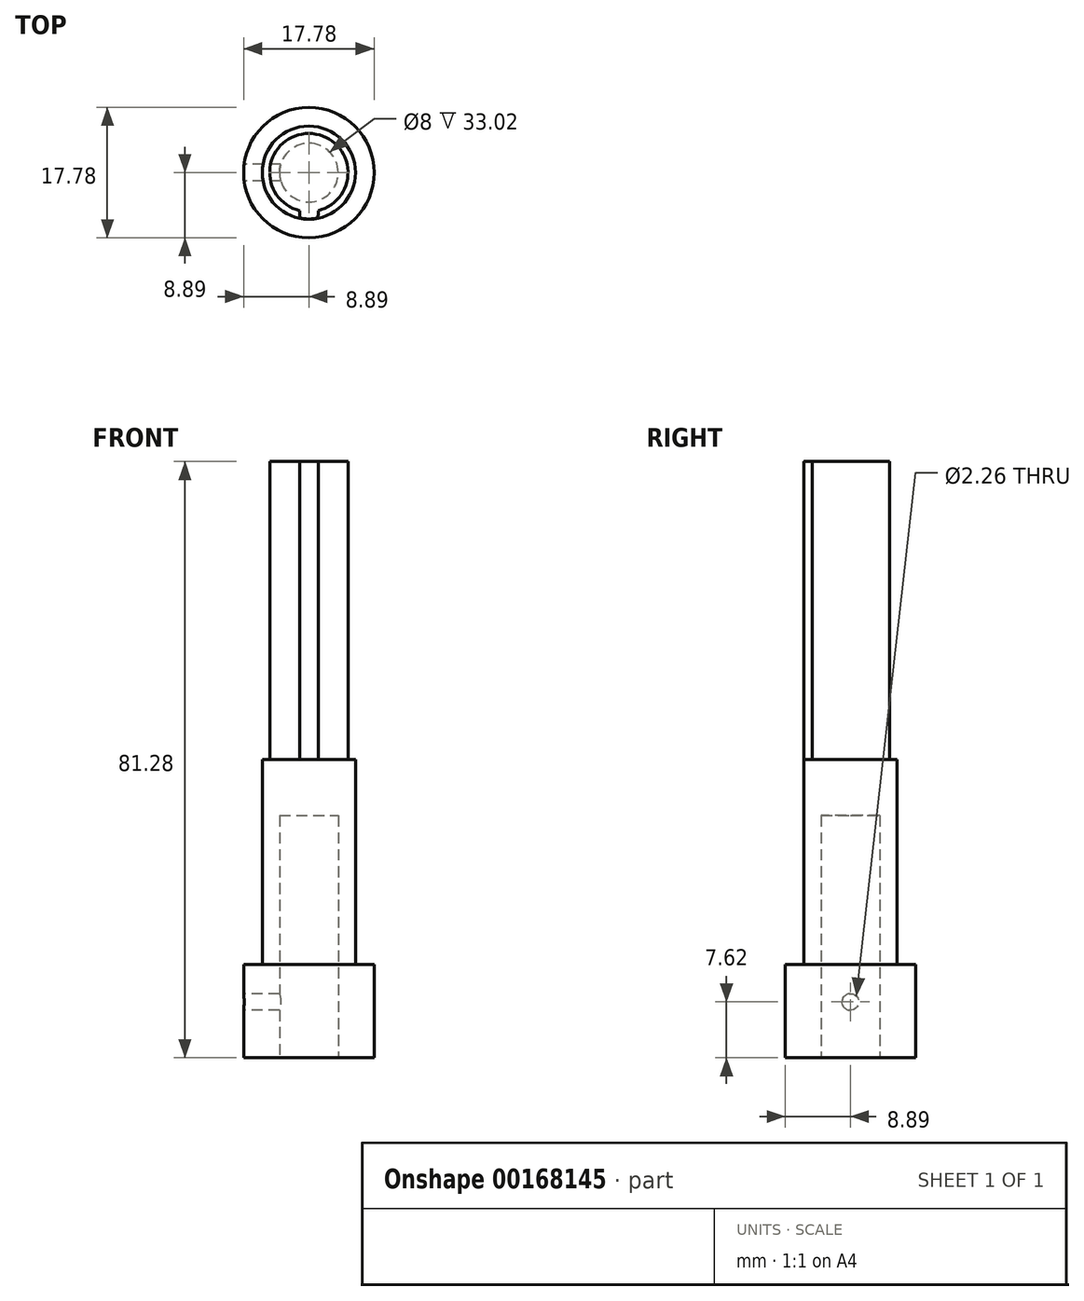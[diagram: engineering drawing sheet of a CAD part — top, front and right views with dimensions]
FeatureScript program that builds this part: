
annotation { "Feature Type Name" : "Feature", "Feature Type Description" : "" }
export const myFeature = defineFeature(function(context is Context, id is Id, definition is map)
    precondition{}
    {
        {
            var Q0;
            Q0=qCreatedBy(makeId("Top.planeOp"),FACE);
            var sketch = newSketch(context, id + "F0", { "sketchPlane" : qUnion([Q0])});
            skCircle(sketch, "E0", {"center": v(0, 0) * mm, "radius": 8.9 * mm});
            skSolve(sketch);
        }
        {
            var Q0;
            Q0=makeQuery(id+"F0.imprint","IMPRINT",FACE,{"disambiguationData":[TD([[makeQuery(id+"F0.imprint","IMPRINT",EDGE,{"derivedFrom":sQuery(id+"F0.wireOp",EDGE,"E0")}),1.0]])]});
            extrude(context, id + "F1", {"entities" : qUnion([Q0]), "depth" : 12.7 * mm});
        }
        {
            var Q0;
            Q0=makeQuery(id+"F1.opExtrude","CAP_FACE",FACE,{"disambiguationData":[OSD([sQuery(id+"F0.wireOp",EDGE,"E0")])],"isStart":false});
            var sketch = newSketch(context, id + "F2", { "sketchPlane" : qUnion([Q0])});
            skCircle(sketch, "E1", {"center": v(0, 0) * mm, "radius": 6.35 * mm});
            skSolve(sketch);
        }
        {
            var Q0;
            Q0=qSketchRegion(id+"F2",true);
            extrude(context, id + "F3", {"entities" : qUnion([Q0]), "operationType" : NewBodyOperationType.ADD, "depth" : 27.94 * mm});
        }
        {
            var Q0;
            Q0=makeQuery(id+"F3.opExtrude","CAP_FACE",FACE,{"disambiguationData":[OSD([sQuery(id+"F2.wireOp",EDGE,"E1")])],"isStart":false});
            var sketch = newSketch(context, id + "F4", { "sketchPlane" : qUnion([Q0])});
            skCircle(sketch, "E2", {"center": v(0, 0) * mm, "radius": 5.33 * mm});
            skSolve(sketch);
        }
        {
            var Q0;
            Q0=qSketchRegion(id+"F4",true);
            extrude(context, id + "F5", {"entities" : qUnion([Q0]), "operationType" : NewBodyOperationType.ADD, "depth" : 40.64 * mm});
        }
        {
            var Q0;
            Q0=makeQuery(id+"F5.opExtrude","CAP_FACE",FACE,{"disambiguationData":[OSD([sQuery(id+"F4.wireOp",EDGE,"E2")])],"isStart":false});
            var sketch = newSketch(context, id + "F6", { "sketchPlane" : qUnion([Q0])});
            skArc(sketch, "E3", {"start": v(-1.27, -6.2) * mm, "mid": v(0, -6.32) * mm, "end": v(1.27, -6.2) * mm});
            skArc(sketch, "E4", {"start": v(-1.27, -5.18) * mm, "mid": v(0, -5.33) * mm, "end": v(1.27, -5.18) * mm});
            skLineSegment(sketch, "E5", {"start": v(-1.27, -6.2) * mm, "end": v(-1.27, -5.18) * mm});
            skLineSegment(sketch, "E6", {"start": v(1.27, -6.2) * mm, "end": v(1.27, -5.18) * mm});
            skSolve(sketch);
        }
        {
            var Q0;
            Q0=qSketchRegion(id+"F6",true);
            var Q1;
            Q1=makeQuery(id+"F3.opExtrude","CAP_FACE",FACE,{"disambiguationData":[OSD([sQuery(id+"F2.wireOp",EDGE,"E1")])],"isStart":false});
            extrude(context, id + "F7", {"entities" : qUnion([Q0]), "operationType" : NewBodyOperationType.ADD, "endBound" : BoundingType.UP_TO_SURFACE, "oppositeDirection" : true, "endBoundEntityFace" : qUnion([Q1]), "depth" : 25.4 * mm});
        }
        {
            var Q0;
            Q0=makeQuery(id+"F7.opExtrude","SWEPT_EDGE",EDGE,{"disambiguationData":[OSD([sQuery(id+"F6.wireOp",EDGE,"E3"),sQuery(id+"F6.wireOp",EDGE,"E6")])]});
            var Q1;
            Q1=makeQuery(id+"F7.opExtrude","SWEPT_EDGE",EDGE,{"disambiguationData":[OSD([sQuery(id+"F4.wireOp",EDGE,"E2"),sQuery(id+"F6.wireOp",EDGE,"E4"),sQuery(id+"F6.wireOp",EDGE,"E6")])]});
            var Q2;
            Q2=makeQuery(id+"F7.opExtrude","SWEPT_EDGE",EDGE,{"disambiguationData":[OSD([sQuery(id+"F6.wireOp",EDGE,"E3"),sQuery(id+"F6.wireOp",EDGE,"E5")])]});
            var Q3;
            Q3=makeQuery(id+"F7.opExtrude","SWEPT_EDGE",EDGE,{"disambiguationData":[OSD([sQuery(id+"F4.wireOp",EDGE,"E2"),sQuery(id+"F6.wireOp",EDGE,"E4"),sQuery(id+"F6.wireOp",EDGE,"E5")])]});
            fillet(context, id + "F8", {"entities" : qUnion([Q0, Q1, Q2, Q3]), "radius" : 0.5 * mm, "tangentPropagation" : true, "allowEdgeOverflow" : false});
        }
        {
            var Q0;
            Q0=makeQuery(id+"F1.opExtrude","CAP_FACE",FACE,{"disambiguationData":[OSD([sQuery(id+"F0.wireOp",EDGE,"E0")])],"isStart":true});
            var sketch = newSketch(context, id + "F9", { "sketchPlane" : qUnion([Q0])});
            skCircle(sketch, "E7", {"center": v(0, 0) * mm, "radius": 4 * mm});
            skSolve(sketch);
        }
        {
            var Q0;
            Q0=makeQuery(id+"F9.imprint","IMPRINT",FACE,{"disambiguationData":[TD([[makeQuery(id+"F9.imprint","IMPRINT",EDGE,{"derivedFrom":sQuery(id+"F9.wireOp",EDGE,"E7")}),1.0]])]});
            extrude(context, id + "F10", {"entities" : qUnion([Q0]), "operationType" : NewBodyOperationType.REMOVE, "oppositeDirection" : true, "depth" : 33.02 * mm});
        }
        {
            var Q0;
            Q0=makeQuery(id+"F1.opExtrude","CAP_FACE",FACE,{"disambiguationData":[OSD([sQuery(id+"F0.wireOp",EDGE,"E0")])],"isStart":false});
            var sketch = newSketch(context, id + "F11", { "sketchPlane" : qUnion([Q0])});
            skCircle(sketch, "E8.0", {"center": v(0, 0) * mm, "radius": 8.9 * mm, "construction": true});
            skPoint(sketch, "E9", {"position": v(-8.9, 0) * mm});
            skSolve(sketch);
        }
        {
            var Q0;
            Q0=sQuery(id+"F11.wireOp",VERTEX,"E9");
            var Q1;
            Q1=qCreatedBy(makeId("Right.planeOp"),FACE);
            cPlane(context, id + "F12", {"entities" : qUnion([Q0, Q1]), "cplaneType" : CPlaneType.PLANE_POINT, "offset" : 25.4 * mm, "width" : 152.4 * mm, "height" : 152.4 * mm});
        }
        {
            var Q0;
            Q0=qCreatedBy(id+"F12.planeOp",FACE);
            var sketch = newSketch(context, id + "F13", { "sketchPlane" : qUnion([Q0])});
            skLineSegment(sketch, "E10", {"start": v(0, 0) * mm, "end": v(0, 7.62) * mm, "construction": true});
            skPoint(sketch, "E11", {"position": v(0, 7.62) * mm});
            skSolve(sketch);
        }
        {
            var Q0;
            Q0=sQuery(id+"F13.wireOp",VERTEX,"E11");
            var Q1;
            Q1=makeQuery(id+"F1.opExtrude","SWEPT_BODY",BODY,{"disambiguationData":[OSD([sQuery(id+"F0.wireOp",EDGE,"E0")])]});
            hole(context, id + "F14", {"style" : HoleStyle.SIMPLE, "endStyle" : HoleEndStyle.BLIND, "oppositeDirection" : true, "standardTappedOrClearance" : lookupTablePath({ "standard" : "ANSI", "engagement" : "75%", "pitch" : "40 tpi", "size" : "#4", "type" : "Tapped" }), "standardBlindInLast" : lookupTablePath({ "standard" : "ANSI", "engagement" : "75%", "pitch" : "40 tpi", "size" : "#4", "type" : "Tapped" }), "holeDiameter" : 2.26 * mm, "holeDepth" : 8.9 * mm, "locations" : qUnion([Q0]), "scope" : qUnion([Q1]), "majorDiameter" : 2.84 * mm});
        }
    });
